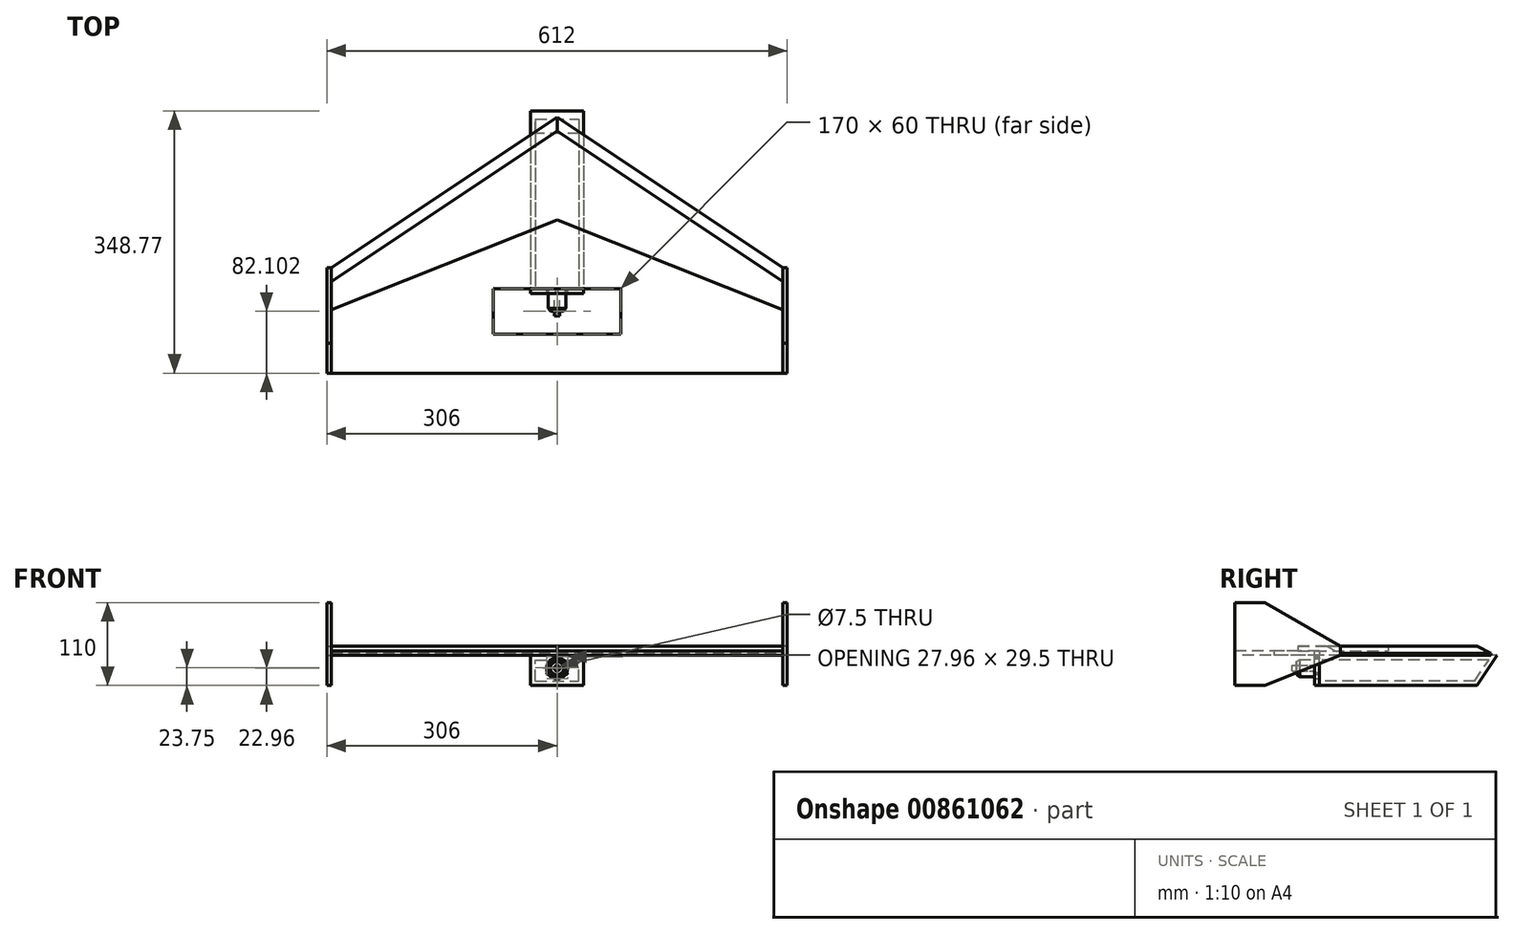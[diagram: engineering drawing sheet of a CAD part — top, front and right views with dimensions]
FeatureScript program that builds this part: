
annotation { "Feature Type Name" : "Feature", "Feature Type Description" : "" }
export const myFeature = defineFeature(function(context is Context, id is Id, definition is map)
    precondition{}
    {
        {
            var Q0;
            Q0=qCreatedBy(makeId("Top.planeOp"),FACE);
            var sketch = newSketch(context, id + "F0", { "sketchPlane" : qUnion([Q0])});
            skLineSegment(sketch, "E0.top", {"start": v(-300, -170) * mm, "end": v(300, -170) * mm});
            skLineSegment(sketch, "E0.left", {"start": v(-300, -30) * mm, "end": v(-300, -170) * mm});
            skLineSegment(sketch, "E0.right", {"start": v(300, -30) * mm, "end": v(300, -170) * mm});
            skPoint(sketch, "E0.middle", {"position": v(0, 0) * mm});
            skLineSegment(sketch, "E1", {"start": v(0, 170) * mm, "end": v(-300, -30) * mm});
            skPoint(sketch, "E2.orphan", {"position": v(-300, 170) * mm});
            skPoint(sketch, "E3.orphan", {"position": v(300, 170) * mm});
            skLineSegment(sketch, "E4", {"start": v(-300, 170) * mm, "end": v(300, 170) * mm, "construction": true});
            skLineSegment(sketch, "E5", {"start": v(-300, -86) * mm, "end": v(0, 34) * mm});
            skLineSegment(sketch, "E6", {"start": v(0, 170) * mm, "end": v(300, -30) * mm});
            skLineSegment(sketch, "E7", {"start": v(0, 34) * mm, "end": v(300, -86) * mm});
            skLineSegment(sketch, "E8.0", {"start": v(0, -170) * mm, "end": v(300, -170) * mm});
            skLineSegment(sketch, "E8.1", {"start": v(-300, -170) * mm, "end": v(0, -170) * mm});
            skLineSegment(sketch, "E9.bottom", {"start": v(-85, -57.9) * mm, "end": v(85, -57.9) * mm});
            skLineSegment(sketch, "E9.top", {"start": v(-85, -117.9) * mm, "end": v(85, -117.9) * mm});
            skLineSegment(sketch, "E9.left", {"start": v(-85, -57.9) * mm, "end": v(-85, -117.9) * mm});
            skLineSegment(sketch, "E9.right", {"start": v(85, -57.9) * mm, "end": v(85, -117.9) * mm});
            skPoint(sketch, "E9.middle", {"position": v(0, -87.9) * mm});
            skLineSegment(sketch, "E10", {"start": v(-300, -130) * mm, "end": v(0, -130) * mm});
            skLineSegment(sketch, "E11", {"start": v(0, -170) * mm, "end": v(0, -130) * mm});
            skPoint(sketch, "E12.orphan", {"position": v(300, -130) * mm});
            skLineSegment(sketch, "E13", {"start": v(0, -130) * mm, "end": v(300, -130) * mm});
            skSolve(sketch);
        }
        {
            var Q0;
            {var subQ0=sQuery(id+"F0.wireOp",EDGE,"E5");Q0=makeQuery(id+"F0.imprint","IMPRINT",FACE,{"disambiguationData":[TD([[makeQuery(id+"F0.imprint","IMPRINT",EDGE,{"derivedFrom":subQ0}),-1.0]])]});}
            var Q1;
            {var subQ4=sQuery(id+"F0.wireOp",EDGE,"E10");Q1=makeQuery(id+"F0.imprint","IMPRINT",FACE,{"disambiguationData":[TD([[makeQuery(id+"F0.imprint","IMPRINT",EDGE,{"derivedFrom":subQ4}),-1.0]])]});}
            var Q2;
            {var subQ0=sQuery(id+"F0.wireOp",EDGE,"E11");Q2=makeQuery(id+"F0.imprint","IMPRINT",FACE,{"disambiguationData":[TD([[makeQuery(id+"F0.imprint","IMPRINT",EDGE,{"derivedFrom":subQ0}),-1.0]])]});}
            extrude(context, id + "F1", {"entities" : qUnion([Q0, Q1, Q2]), "depth" : 6 * mm, "offsetDistance" : 25 * mm});
        }
        {
            var Q0;
            {var subQ1=sQuery(id+"F0.wireOp",EDGE,"E1");Q0=makeQuery(id+"F0.imprint","IMPRINT",FACE,{"disambiguationData":[TD([[makeQuery(id+"F0.imprint","IMPRINT",EDGE,{"derivedFrom":subQ1}),1.0]])]});}
            extrude(context, id + "F2", {"entities" : qUnion([Q0]), "operationType" : NewBodyOperationType.ADD, "depth" : 12 * mm, "offsetDistance" : 25 * mm});
        }
        {
            var Q0;
            Q0=makeQuery(id+"F2.opExtrude","CAP_EDGE",EDGE,{"disambiguationData":[OSD([sQuery(id+"F0.wireOp",EDGE,"E1")])],"isStart":false});
            var Q1;
            Q1=makeQuery(id+"F2.opExtrude","CAP_EDGE",EDGE,{"disambiguationData":[OSD([sQuery(id+"F0.wireOp",EDGE,"E6")])],"isStart":false});
            chamfer(context, id + "F3", {"entities" : qUnion([Q0, Q1]), "chamferType" : ChamferType.TWO_OFFSETS, "width1" : 15 * mm, "oppositeDirection" : false, "width2" : 9 * mm, "tangentPropagation" : true});
        }
        {
            var Q0;
            Q0=makeQuery(id+"F0.imprint","IMPRINT",FACE,{"disambiguationData":[TD([[makeQuery(id+"F0.imprint","IMPRINT",EDGE,{"derivedFrom":sQuery(id+"F0.wireOp",EDGE,"E9.bottom")}),-1.0]])]});
            var sketch = newSketch(context, id + "F4", { "sketchPlane" : qUnion([Q0])});
            skLineSegment(sketch, "E14.bottom", {"start": v(-35, 192.1) * mm, "end": v(35, 192.1) * mm});
            skLineSegment(sketch, "E14.top", {"start": v(-35, -57.9) * mm, "end": v(35, -57.9) * mm});
            skLineSegment(sketch, "E14.left", {"start": v(-35, 192.1) * mm, "end": v(-35, -57.9) * mm});
            skLineSegment(sketch, "E14.right", {"start": v(35, 192.1) * mm, "end": v(35, -57.9) * mm});
            skPoint(sketch, "E14.middle", {"position": v(0, 67.1) * mm});
            skSolve(sketch);
        }
        {
            var Q0;
            Q0 = qSketchRegion(id + "F4", true);
            extrude(context, id + "F5", {"entities" : qUnion([Q0]), "oppositeDirection" : true, "depth" : 40 * mm, "offsetDistance" : 25 * mm});
        }
        {
            var Q0;
            Q0=makeQuery(id+"F5.opExtrude","CAP_EDGE",EDGE,{"disambiguationData":[OSD([sQuery(id+"F4.wireOp",EDGE,"E14.bottom")])],"isStart":false});
            chamfer(context, id + "F6", {"entities" : qUnion([Q0]), "chamferType" : ChamferType.TWO_OFFSETS, "width1" : 60 * mm, "oppositeDirection" : false, "width2" : 40 * mm, "tangentPropagation" : true});
        }
        {
            var Q0;
            {var subQ0=sQuery(id+"F0.wireOp",EDGE,"E0.right");Q0=makeQuery(id+"F2.boolean.opBoolean","MERGE",FACE,{"derivedFrom":[makeQuery(id+"F1.opExtrude","SWEPT_FACE",FACE,{"disambiguationData":[OSD([subQ0])]}),makeQuery(id+"F2.opExtrude","SWEPT_FACE",FACE,{"disambiguationData":[OSD([subQ0])]})]});}
            var sketch = newSketch(context, id + "F7", { "sketchPlane" : qUnion([Q0])});
            skLineSegment(sketch, "E15", {"start": v(-170, 70) * mm, "end": v(-170, 0) * mm});
            skLineSegment(sketch, "E16", {"start": v(-170, 70) * mm, "end": v(-130, 70) * mm});
            skLineSegment(sketch, "E17", {"start": v(-170, 0) * mm, "end": v(-170, -40) * mm});
            skLineSegment(sketch, "E18", {"start": v(-170, -40) * mm, "end": v(-130, -40) * mm});
            skLineSegment(sketch, "E19", {"start": v(-170, 0) * mm, "end": v(-30, 0) * mm});
            skLineSegment(sketch, "E20", {"start": v(-130, -40) * mm, "end": v(-30, 0) * mm});
            skLineSegment(sketch, "E21", {"start": v(-30, 0) * mm, "end": v(-30, 12) * mm});
            skLineSegment(sketch, "E22", {"start": v(-30, 12) * mm, "end": v(-130, 70) * mm});
            skSolve(sketch);
        }
        {
            var Q0;
            Q0=makeQuery(id+"F7.imprint","IMPRINT",FACE,{"disambiguationData":[TD([[makeQuery(id+"F7.imprint","IMPRINT",EDGE,{"derivedFrom":sQuery(id+"F7.wireOp",EDGE,"E17")}),1.0]])]});
            var Q1;
            {var subQ4=sQuery(id+"F7.wireOp",EDGE,"E16");Q1=makeQuery(id+"F7.imprint","IMPRINT",FACE,{"disambiguationData":[TD([[makeQuery(id+"F7.imprint","IMPRINT",EDGE,{"derivedFrom":subQ4}),-1.0]])]});}
            var Q2;
            {var subQ1=sQuery(id+"F7.wireOp",EDGE,"E19");Q2=makeQuery(id+"F7.imprint","IMPRINT",FACE,{"disambiguationData":[TD([[makeQuery(id+"F7.imprint","IMPRINT",EDGE,{"derivedFrom":subQ1}),-1.0]])]});}
            var Q3;
            Q3 = qSketchRegion(id + "F9", true);
            extrude(context, id + "F8", {"entities" : qUnion([Q0, Q1, Q2, Q3]), "depth" : 6 * mm, "offsetDistance" : 25 * mm});
        }
        {
            var Q0;
            {var subQ0=sQuery(id+"F0.wireOp",EDGE,"E0.left");Q0=makeQuery(id+"F2.boolean.opBoolean","MERGE",FACE,{"derivedFrom":[makeQuery(id+"F1.opExtrude","SWEPT_FACE",FACE,{"disambiguationData":[OSD([subQ0])]}),makeQuery(id+"F2.opExtrude","SWEPT_FACE",FACE,{"disambiguationData":[OSD([subQ0])]})]});}
            var sketch = newSketch(context, id + "F9", { "sketchPlane" : qUnion([Q0])});
            skLineSegment(sketch, "E23", {"start": v(170, 0) * mm, "end": v(30, 0) * mm});
            skLineSegment(sketch, "E24", {"start": v(30, 0) * mm, "end": v(30, 12) * mm});
            skLineSegment(sketch, "E25", {"start": v(30, 12) * mm, "end": v(130, 70) * mm});
            skLineSegment(sketch, "E26", {"start": v(130, 70) * mm, "end": v(170, 70) * mm});
            skLineSegment(sketch, "E27", {"start": v(170, 70) * mm, "end": v(170, 0) * mm});
            skLineSegment(sketch, "E28", {"start": v(170, 0) * mm, "end": v(170, -40) * mm});
            skLineSegment(sketch, "E29", {"start": v(170, -40) * mm, "end": v(130, -40) * mm});
            skLineSegment(sketch, "E30", {"start": v(130, -40) * mm, "end": v(30, 0) * mm});
            skSolve(sketch);
        }
        {
            var Q0;
            Q0=makeQuery(id+"F9.imprint","IMPRINT",FACE,{"disambiguationData":[TD([[makeQuery(id+"F9.imprint","IMPRINT",EDGE,{"derivedFrom":sQuery(id+"F9.wireOp",EDGE,"E23")}),-1.0]])]});
            var Q1;
            {var subQ4=sQuery(id+"F9.wireOp",EDGE,"E25");Q1=makeQuery(id+"F9.imprint","IMPRINT",FACE,{"disambiguationData":[TD([[makeQuery(id+"F9.imprint","IMPRINT",EDGE,{"derivedFrom":subQ4}),-1.0]])]});}
            var Q2;
            {var subQ1=sQuery(id+"F9.wireOp",EDGE,"E23");Q2=makeQuery(id+"F9.imprint","IMPRINT",FACE,{"disambiguationData":[TD([[makeQuery(id+"F9.imprint","IMPRINT",EDGE,{"derivedFrom":subQ1}),1.0]])]});}
            extrude(context, id + "F10", {"entities" : qUnion([Q0, Q1, Q2]), "depth" : 6 * mm, "offsetDistance" : 25 * mm});
        }
        {
            var Q0;
            Q0=makeQuery(id+"F5.opExtrude","SWEPT_FACE",FACE,{"disambiguationData":[OSD([sQuery(id+"F4.wireOp",EDGE,"E14.top")])]});
            var sketch = newSketch(context, id + "F11", { "sketchPlane" : qUnion([Q0])});
            skLineSegment(sketch, "E31", {"start": v(-35, -40) * mm, "end": v(35, -40) * mm});
            skLineSegment(sketch, "E32", {"start": v(35, -40) * mm, "end": v(35, 6) * mm});
            skLineSegment(sketch, "E33", {"start": v(35, 6) * mm, "end": v(-35, 6) * mm});
            skLineSegment(sketch, "E34", {"start": v(-35, 6) * mm, "end": v(-35, -40) * mm});
            skCircle(sketch, "E35", {"center": v(0, -17) * mm, "radius": 14 * mm});
            skPoint(sketch, "E35.centerSnap0", {"position": v(-35, -17) * mm});
            skCircle(sketch, "E36", {"center": v(0, -3) * mm, "radius": 1.5 * mm});
            skCircle(sketch, "E37.1.0", {"center": v(-12.12, -24) * mm, "radius": 1.5 * mm});
            skCircle(sketch, "E37.2.0", {"center": v(12.12, -24) * mm, "radius": 1.5 * mm});
            skCircle(sketch, "E38", {"center": v(0, -17) * mm, "radius": 2.5 * mm});
            skSolve(sketch);
        }
        {
            var Q0;
            {var subQ7=sQuery(id+"F11.wireOp",EDGE,"E31");Q0=makeQuery(id+"F11.imprint","IMPRINT",FACE,{"disambiguationData":[TD([[makeQuery(id+"F11.imprint","IMPRINT",EDGE,{"derivedFrom":subQ7}),1.0]])]});}
            var Q1;
            {var subQ0=sQuery(id+"F11.wireOp",EDGE,"E36");var subQ1=sQuery(id+"F11.wireOp",EDGE,"E35");var subQ8=makeQuery(id+"F11.imprint","INTERSECT",VERTEX,{"disambiguationData":[OD(0.0)],"derivedFrom":[subQ1,subQ0]});Q1=makeQuery(id+"F11.imprint","IMPRINT",FACE,{"disambiguationData":[TD([[makeQuery(id+"F11.imprint","IMPRINT",EDGE,{"disambiguationData":[TD([[subQ8,-1.0]])],"derivedFrom":subQ1}),1.0]])]});}
            var Q2;
            {var subQ2=sQuery(id+"F11.wireOp",EDGE,"E33");Q2=makeQuery(id+"F11.imprint","IMPRINT",FACE,{"disambiguationData":[TD([[makeQuery(id+"F11.imprint","IMPRINT",EDGE,{"derivedFrom":subQ2}),1.0]])]});}
            extrude(context, id + "F12", {"entities" : qUnion([Q0, Q1, Q2]), "depth" : 6 * mm, "offsetDistance" : 25 * mm});
        }
        {
            var Q0;
            Q0=makeQuery(id+"F12.opExtrude","CAP_FACE",FACE,{"disambiguationData":[OSD([sQuery(id+"F11.wireOp",EDGE,"E31"),sQuery(id+"F11.wireOp",EDGE,"E32"),sQuery(id+"F11.wireOp",EDGE,"E33"),sQuery(id+"F11.wireOp",EDGE,"E34"),sQuery(id+"F11.wireOp",EDGE,"E36"),sQuery(id+"F11.wireOp",EDGE,"E37.1.0"),sQuery(id+"F11.wireOp",EDGE,"E37.2.0")])],"isStart":false});
            var sketch = newSketch(context, id + "F13", { "sketchPlane" : qUnion([Q0])});
            skCircle(sketch, "E39", {"center": v(0, -17.04) * mm, "radius": 11.5 * mm});
            skCircle(sketch, "E40", {"center": v(0, -17.04) * mm, "radius": 3.75 * mm});
            skSolve(sketch);
        }
        {
            var Q0;
            Q0=makeQuery(id+"F13.imprint","IMPRINT",FACE,{"disambiguationData":[TD([[makeQuery(id+"F13.imprint","IMPRINT",EDGE,{"derivedFrom":sQuery(id+"F13.wireOp",EDGE,"E39")}),1.0]])]});
            extrude(context, id + "F14", {"entities" : qUnion([Q0]), "depth" : 24 * mm, "offsetDistance" : 25 * mm});
        }
        {
            var Q0;
            Q0=makeQuery(id+"F14.opExtrude","CAP_EDGE",EDGE,{"disambiguationData":[OSD([sQuery(id+"F13.wireOp",EDGE,"E39")])],"isStart":false});
            chamfer(context, id + "F15", {"entities" : qUnion([Q0]), "chamferType" : ChamferType.OFFSET_ANGLE, "width" : 4 * mm, "oppositeDirection" : false, "angle" : 35 * degree, "tangentPropagation" : true});
        }
        {
            var Q0;
            Q0=makeQuery(id+"F13.imprint","IMPRINT",FACE,{"disambiguationData":[TD([[makeQuery(id+"F13.imprint","IMPRINT",EDGE,{"derivedFrom":sQuery(id+"F13.wireOp",EDGE,"E40")}),1.0]])]});
            var Q1;
            Q1=makeQuery(id+"F13.imprint","IMPRINT",FACE,{"disambiguationData":[TD([[makeQuery(id+"F13.imprint","IMPRINT",EDGE,{"derivedFrom":makeQuery(id+"F12.opExtrude","CAP_EDGE",EDGE,{"disambiguationData":[OSD([sQuery(id+"F11.wireOp",EDGE,"E38")])],"isStart":false})}),1.0]])]});
            extrude(context, id + "F16", {"entities" : qUnion([Q0, Q1]), "depth" : 30 * mm, "offsetDistance" : 25 * mm});
        }
        {
            var Q0;
            Q0=makeQuery(id+"F5.opExtrude","SWEPT_FACE",FACE,{"disambiguationData":[OSD([sQuery(id+"F4.wireOp",EDGE,"E14.top")])]});
            shell(context, id + "F17", {"entities" : qUnion([Q0]), "thickness" : 6 * mm});
        }
    });
